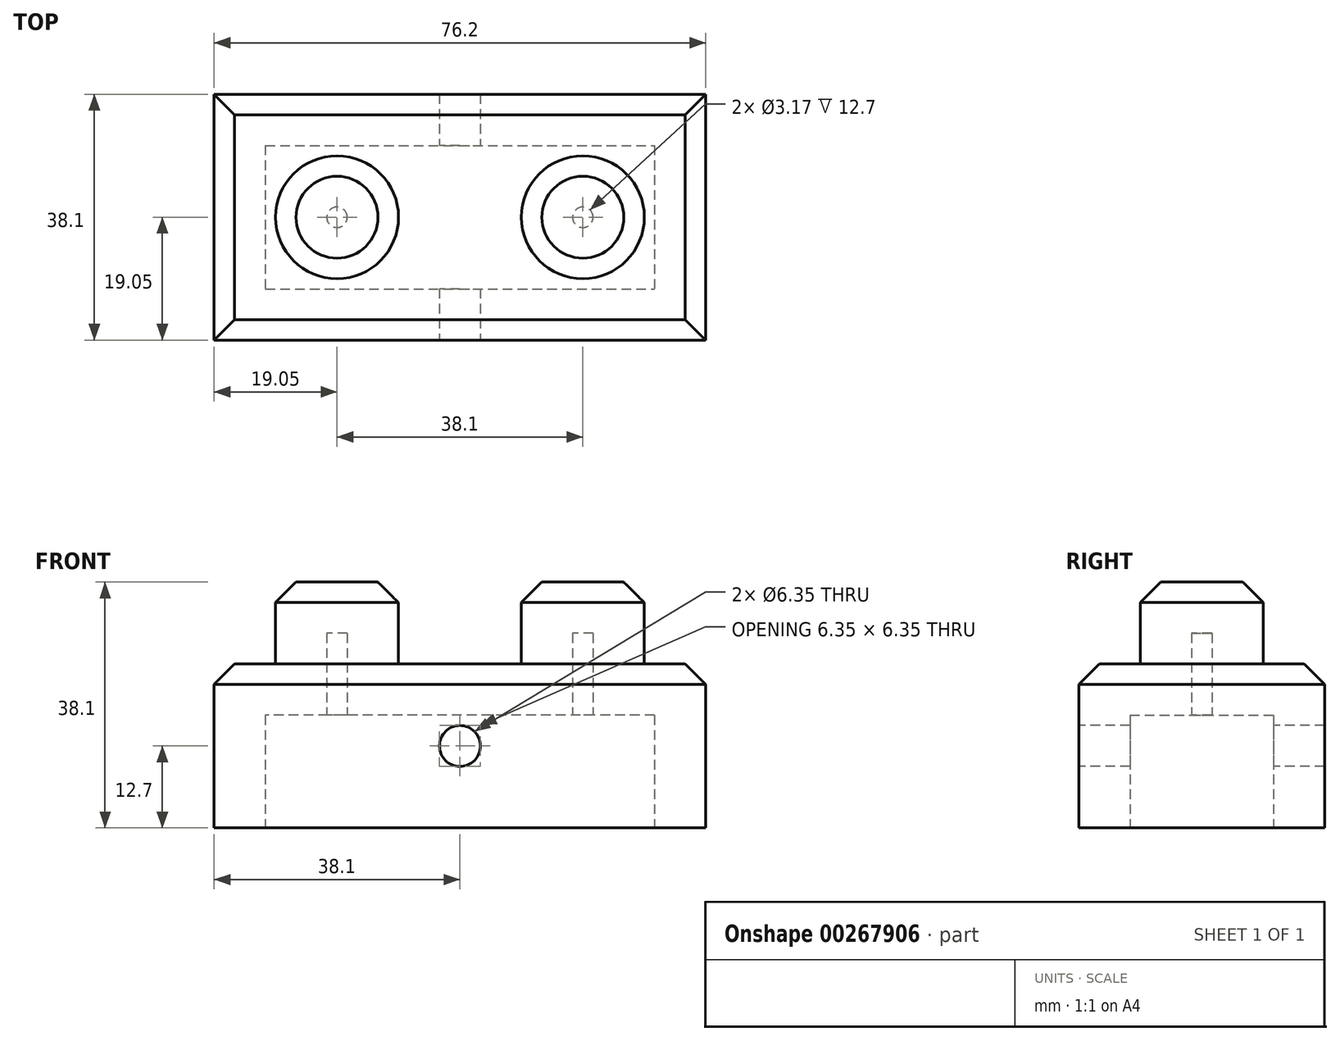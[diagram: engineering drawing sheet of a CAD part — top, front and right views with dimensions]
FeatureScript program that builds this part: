
annotation { "Feature Type Name" : "Feature", "Feature Type Description" : "" }
export const myFeature = defineFeature(function(context is Context, id is Id, definition is map)
    precondition{}
    {
        {
            var Q0;
            Q0=qCreatedBy(makeId("Top.planeOp"),FACE);
            var sketch = newSketch(context, id + "F0", { "sketchPlane" : qUnion([Q0])});
            skLineSegment(sketch, "E0.bottom", {"start": v(0, 0) * mm, "end": v(76.2, 0) * mm});
            skLineSegment(sketch, "E0.top", {"start": v(0, -38.1) * mm, "end": v(76.2, -38.1) * mm});
            skLineSegment(sketch, "E0.left", {"start": v(0, 0) * mm, "end": v(0, -38.1) * mm});
            skLineSegment(sketch, "E0.right", {"start": v(76.2, 0) * mm, "end": v(76.2, -38.1) * mm});
            skSolve(sketch);
        }
        {
            var Q0;
            Q0=makeQuery(id+"F0.imprint","IMPRINT",FACE,{"disambiguationData":[TD([[makeQuery(id+"F0.imprint","IMPRINT",EDGE,{"derivedFrom":sQuery(id+"F0.wireOp",EDGE,"E0.bottom")}),-1.0]])]});
            extrude(context, id + "F1", {"entities" : qUnion([Q0]), "depth" : 25.4 * mm});
        }
        {
            var Q0;
            Q0=makeQuery(id+"F1.opExtrude","CAP_FACE",FACE,{"disambiguationData":[OSD([sQuery(id+"F0.wireOp",EDGE,"E0.bottom"),sQuery(id+"F0.wireOp",EDGE,"E0.top"),sQuery(id+"F0.wireOp",EDGE,"E0.left"),sQuery(id+"F0.wireOp",EDGE,"E0.right")])],"isStart":false});
            var sketch = newSketch(context, id + "F2", { "sketchPlane" : qUnion([Q0])});
            skCircle(sketch, "E1", {"center": v(57.15, -19.05) * mm, "radius": 9.53 * mm});
            skCircle(sketch, "E2", {"center": v(19.05, -19.05) * mm, "radius": 9.53 * mm});
            skSolve(sketch);
        }
        {
            var Q0;
            Q0=qSketchRegion(id+"F2",true);
            extrude(context, id + "F3", {"entities" : qUnion([Q0]), "operationType" : NewBodyOperationType.ADD, "depth" : 12.7 * mm});
        }
        {
            var Q0;
            Q0=makeQuery(id+"F3.opExtrude","CAP_EDGE",EDGE,{"disambiguationData":[OSD([sQuery(id+"F2.wireOp",EDGE,"E2")])],"isStart":false});
            var Q1;
            Q1=makeQuery(id+"F3.opExtrude","CAP_EDGE",EDGE,{"disambiguationData":[OSD([sQuery(id+"F2.wireOp",EDGE,"E1")])],"isStart":false});
            var Q2;
            Q2=makeQuery(id+"F1.opExtrude","CAP_EDGE",EDGE,{"disambiguationData":[OSD([sQuery(id+"F0.wireOp",EDGE,"E0.right")])],"isStart":false});
            var Q3;
            Q3=makeQuery(id+"F1.opExtrude","CAP_EDGE",EDGE,{"disambiguationData":[OSD([sQuery(id+"F0.wireOp",EDGE,"E0.top")])],"isStart":false});
            var Q4;
            Q4=makeQuery(id+"F1.opExtrude","CAP_EDGE",EDGE,{"disambiguationData":[OSD([sQuery(id+"F0.wireOp",EDGE,"E0.left")])],"isStart":false});
            var Q5;
            Q5=makeQuery(id+"F1.opExtrude","CAP_EDGE",EDGE,{"disambiguationData":[OSD([sQuery(id+"F0.wireOp",EDGE,"E0.bottom")])],"isStart":false});
            chamfer(context, id + "F4", {"entities" : qUnion([Q0, Q1, Q2, Q3, Q4, Q5]), "chamferType" : ChamferType.OFFSET_ANGLE, "width" : 3.17 * mm, "oppositeDirection" : false, "angle" : 45 * degree, "tangentPropagation" : true});
        }
        {
            var Q0;
            Q0=makeQuery(id+"F1.opExtrude","CAP_FACE",FACE,{"disambiguationData":[OSD([sQuery(id+"F0.wireOp",EDGE,"E0.bottom"),sQuery(id+"F0.wireOp",EDGE,"E0.top"),sQuery(id+"F0.wireOp",EDGE,"E0.left"),sQuery(id+"F0.wireOp",EDGE,"E0.right")])],"isStart":true});
            shell(context, id + "F5", {"entities" : qUnion([Q0]), "thickness" : 7.94 * mm});
        }
        {
            var Q0;
            Q0=makeQuery(id+"F1.opExtrude","SWEPT_FACE",FACE,{"disambiguationData":[OSD([sQuery(id+"F0.wireOp",EDGE,"E0.top")])]});
            var sketch = newSketch(context, id + "F6", { "sketchPlane" : qUnion([Q0])});
            skCircle(sketch, "E3", {"center": v(38.1, 12.7) * mm, "radius": 3.18 * mm});
            skSolve(sketch);
        }
        {
            var Q0;
            Q0=qSketchRegion(id+"F6",true);
            extrude(context, id + "F7", {"entities" : qUnion([Q0]), "operationType" : NewBodyOperationType.REMOVE, "oppositeDirection" : true, "depth" : 38.1 * mm});
        }
    });
